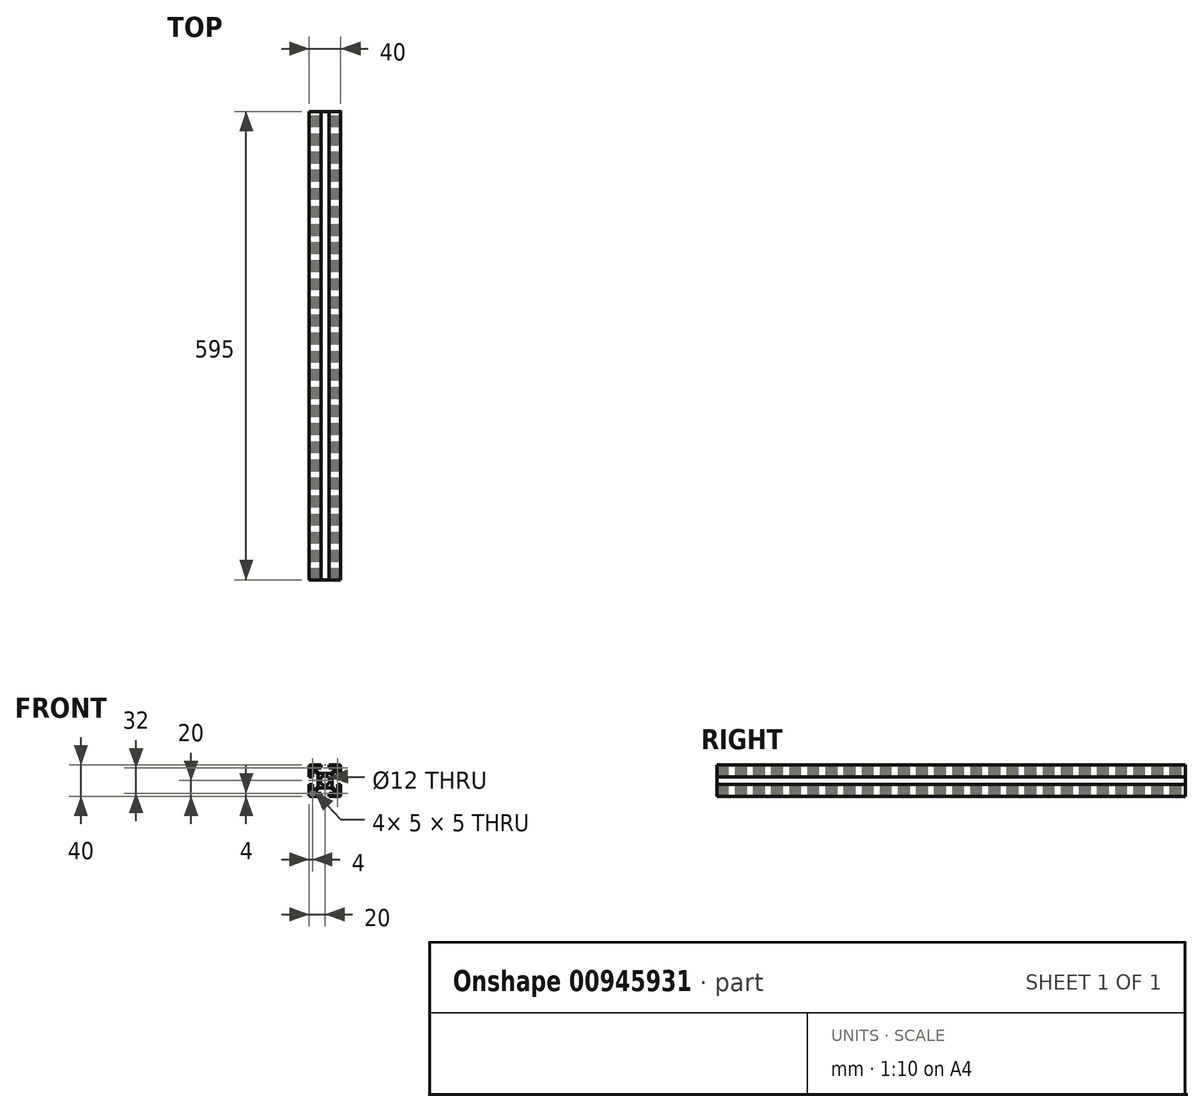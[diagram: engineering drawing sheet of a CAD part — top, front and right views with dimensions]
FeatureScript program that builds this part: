
annotation { "Feature Type Name" : "Feature", "Feature Type Description" : "" }
export const myFeature = defineFeature(function(context is Context, id is Id, definition is map)
    precondition{}
    {
        {
            var Q0;
            Q0=qCreatedBy(makeId("Front.planeOp"),FACE);
            var sketch = newSketch(context, id + "F0", { "sketchPlane" : qUnion([Q0])});
            skLineSegment(sketch, "E0.bottom", {"start": v(18, -20) * mm, "end": v(5, -20) * mm});
            skLineSegment(sketch, "E0.top", {"start": v(18, 20) * mm, "end": v(5, 20) * mm});
            skLineSegment(sketch, "E0.left", {"start": v(20, -18) * mm, "end": v(20, -5) * mm});
            skLineSegment(sketch, "E0.right", {"start": v(-20, -18) * mm, "end": v(-20, -5) * mm});
            skPoint(sketch, "E0.middle", {"position": v(0, 0) * mm});
            skLineSegment(sketch, "E1", {"start": v(0, 20) * mm, "end": v(0, -20) * mm, "construction": true});
            skLineSegment(sketch, "E2", {"start": v(-5, 20) * mm, "end": v(-5, 16) * mm});
            skLineSegment(sketch, "E3", {"start": v(-5, 16) * mm, "end": v(-11.5, 16) * mm});
            skCircle(sketch, "E4", {"center": v(0, 0) * mm, "radius": 6 * mm});
            skPoint(sketch, "E5.visualSharp", {"position": v(-20, 20) * mm});
            skArc(sketch, "E5.filletArc", {"start": v(-18, 20) * mm, "mid": v(-19.41, 19.41) * mm, "end": v(-20, 18) * mm});
            skPoint(sketch, "E6.visualSharp", {"position": v(20, 20) * mm});
            skArc(sketch, "E6.filletArc", {"start": v(20, 18) * mm, "mid": v(19.41, 19.41) * mm, "end": v(18, 20) * mm});
            skPoint(sketch, "E7.visualSharp", {"position": v(20, -20) * mm});
            skArc(sketch, "E7.filletArc", {"start": v(18, -20) * mm, "mid": v(19.41, -19.41) * mm, "end": v(20, -18) * mm});
            skPoint(sketch, "E8.visualSharp", {"position": v(-20, -20) * mm});
            skArc(sketch, "E8.filletArc", {"start": v(-20, -18) * mm, "mid": v(-19.41, -19.41) * mm, "end": v(-18, -20) * mm});
            skLineSegment(sketch, "E9", {"start": v(-7, 7) * mm, "end": v(-18, 18) * mm, "construction": true});
            skLineSegment(sketch, "E10.bottom", {"start": v(-13.5, 13.5) * mm, "end": v(-18.5, 13.5) * mm});
            skLineSegment(sketch, "E10.top", {"start": v(-13.5, 18.5) * mm, "end": v(-18.5, 18.5) * mm});
            skLineSegment(sketch, "E10.left", {"start": v(-13.5, 13.5) * mm, "end": v(-13.5, 18.5) * mm});
            skLineSegment(sketch, "E10.right", {"start": v(-18.5, 13.5) * mm, "end": v(-18.5, 18.5) * mm});
            skPoint(sketch, "E10.middle", {"position": v(-16, 16) * mm});
            skLineSegment(sketch, "E11.MirrorCS", {"start": v(5, 20) * mm, "end": v(5, 16) * mm});
            skLineSegment(sketch, "E12.MirrorCS", {"start": v(5, 16) * mm, "end": v(11.5, 16) * mm});
            skLineSegment(sketch, "E13.MirrorCS", {"start": v(13.5, 13.5) * mm, "end": v(18.5, 13.5) * mm});
            skLineSegment(sketch, "E14.MirrorCS", {"start": v(18.5, 13.5) * mm, "end": v(18.5, 18.5) * mm});
            skLineSegment(sketch, "E15.MirrorCS", {"start": v(13.5, 18.5) * mm, "end": v(18.5, 18.5) * mm});
            skLineSegment(sketch, "E16.MirrorCS", {"start": v(13.5, 13.5) * mm, "end": v(13.5, 18.5) * mm});
            skLineSegment(sketch, "E17", {"start": v(-20, 0) * mm, "end": v(20, 0) * mm, "construction": true});
            skLineSegment(sketch, "E18.trimOffspring", {"start": v(-5, 20) * mm, "end": v(-18, 20) * mm});
            skLineSegment(sketch, "E19", {"start": v(-11.5, 16) * mm, "end": v(-11.5, 12.91) * mm});
            skLineSegment(sketch, "E20", {"start": v(-11.5, 12.91) * mm, "end": v(-7.59, 9) * mm});
            skLineSegment(sketch, "E21", {"start": v(-7.59, 9) * mm, "end": v(0, 9) * mm});
            skLineSegment(sketch, "E22.MirrorCS", {"start": v(11.5, 16) * mm, "end": v(11.5, 12.91) * mm});
            skLineSegment(sketch, "E23.MirrorCS", {"start": v(11.5, 12.91) * mm, "end": v(7.59, 9) * mm});
            skLineSegment(sketch, "E24.MirrorCS", {"start": v(7.59, 9) * mm, "end": v(0, 9) * mm});
            skLineSegment(sketch, "E25.1.0", {"start": v(-20, -5) * mm, "end": v(-16, -5) * mm});
            skLineSegment(sketch, "E25.1.1", {"start": v(-16, -5) * mm, "end": v(-16, -11.5) * mm});
            skLineSegment(sketch, "E25.1.2", {"start": v(-16, -11.5) * mm, "end": v(-12.91, -11.5) * mm});
            skLineSegment(sketch, "E25.1.3", {"start": v(-12.91, -11.5) * mm, "end": v(-9, -7.59) * mm});
            skLineSegment(sketch, "E25.1.4", {"start": v(-9, -7.59) * mm, "end": v(-9, 0) * mm});
            skLineSegment(sketch, "E25.1.5", {"start": v(-9, 7.59) * mm, "end": v(-9, 0) * mm});
            skLineSegment(sketch, "E25.1.6", {"start": v(-12.91, 11.5) * mm, "end": v(-9, 7.59) * mm});
            skLineSegment(sketch, "E25.1.7", {"start": v(-16, 11.5) * mm, "end": v(-12.91, 11.5) * mm});
            skLineSegment(sketch, "E25.1.8", {"start": v(-16, 5) * mm, "end": v(-16, 11.5) * mm});
            skLineSegment(sketch, "E25.1.9", {"start": v(-20, 5) * mm, "end": v(-16, 5) * mm});
            skLineSegment(sketch, "E25.2.0", {"start": v(5, -20) * mm, "end": v(5, -16) * mm});
            skLineSegment(sketch, "E25.2.1", {"start": v(5, -16) * mm, "end": v(11.5, -16) * mm});
            skLineSegment(sketch, "E25.2.2", {"start": v(11.5, -16) * mm, "end": v(11.5, -12.91) * mm});
            skLineSegment(sketch, "E25.2.3", {"start": v(11.5, -12.91) * mm, "end": v(7.59, -9) * mm});
            skLineSegment(sketch, "E25.2.4", {"start": v(7.59, -9) * mm, "end": v(0, -9) * mm});
            skLineSegment(sketch, "E25.2.5", {"start": v(-7.59, -9) * mm, "end": v(0, -9) * mm});
            skLineSegment(sketch, "E25.2.6", {"start": v(-11.5, -12.91) * mm, "end": v(-7.59, -9) * mm});
            skLineSegment(sketch, "E25.2.7", {"start": v(-11.5, -16) * mm, "end": v(-11.5, -12.91) * mm});
            skLineSegment(sketch, "E25.2.8", {"start": v(-5, -16) * mm, "end": v(-11.5, -16) * mm});
            skLineSegment(sketch, "E25.2.9", {"start": v(-5, -20) * mm, "end": v(-5, -16) * mm});
            skLineSegment(sketch, "E26.2.3.0", {"start": v(20, 5) * mm, "end": v(16, 5) * mm});
            skLineSegment(sketch, "E26.3.3.0", {"start": v(16, 5) * mm, "end": v(16, 11.5) * mm});
            skLineSegment(sketch, "E26.6.3.0", {"start": v(16, 11.5) * mm, "end": v(12.91, 11.5) * mm});
            skLineSegment(sketch, "E26.9.3.0", {"start": v(12.91, 11.5) * mm, "end": v(9, 7.59) * mm});
            skLineSegment(sketch, "E26.12.3.0", {"start": v(9, 7.59) * mm, "end": v(9, 0) * mm});
            skLineSegment(sketch, "E26.15.3.0", {"start": v(9, -7.59) * mm, "end": v(9, 0) * mm});
            skLineSegment(sketch, "E26.18.3.0", {"start": v(12.91, -11.5) * mm, "end": v(9, -7.59) * mm});
            skLineSegment(sketch, "E26.21.3.0", {"start": v(16, -11.5) * mm, "end": v(12.91, -11.5) * mm});
            skLineSegment(sketch, "E26.24.3.0", {"start": v(16, -5) * mm, "end": v(16, -11.5) * mm});
            skLineSegment(sketch, "E26.27.3.0", {"start": v(20, -5) * mm, "end": v(16, -5) * mm});
            skLineSegment(sketch, "E27.trimOffspring", {"start": v(-20, 5) * mm, "end": v(-20, 18) * mm});
            skLineSegment(sketch, "E28.trimOffspring", {"start": v(-5, -20) * mm, "end": v(-18, -20) * mm});
            skLineSegment(sketch, "E29.trimOffspring", {"start": v(20, 5) * mm, "end": v(20, 18) * mm});
            skLineSegment(sketch, "E30.MirrorCS", {"start": v(-18.5, -13.5) * mm, "end": v(-18.5, -18.5) * mm});
            skLineSegment(sketch, "E31.MirrorCS", {"start": v(-13.5, -18.5) * mm, "end": v(-18.5, -18.5) * mm});
            skLineSegment(sketch, "E32.MirrorCS", {"start": v(-13.5, -13.5) * mm, "end": v(-13.5, -18.5) * mm});
            skLineSegment(sketch, "E33.MirrorCS", {"start": v(-13.5, -13.5) * mm, "end": v(-18.5, -13.5) * mm});
            skLineSegment(sketch, "E34.MirrorCS", {"start": v(13.5, -13.5) * mm, "end": v(13.5, -18.5) * mm});
            skLineSegment(sketch, "E35.MirrorCS", {"start": v(13.5, -18.5) * mm, "end": v(18.5, -18.5) * mm});
            skLineSegment(sketch, "E36.MirrorCS", {"start": v(18.5, -13.5) * mm, "end": v(18.5, -18.5) * mm});
            skLineSegment(sketch, "E37.MirrorCS", {"start": v(13.5, -13.5) * mm, "end": v(18.5, -13.5) * mm});
            skSolve(sketch);
        }
        {
            var Q0;
            Q0=makeQuery(id+"F0.imprint","IMPRINT",FACE,{"disambiguationData":[TD([[makeQuery(id+"F0.imprint","IMPRINT",EDGE,{"derivedFrom":sQuery(id+"F0.wireOp",EDGE,"E0.bottom")}),-1.0]])]});
            extrude(context, id + "F1", {"entities" : qUnion([Q0]), "depth" : 595 * mm, "offsetDistance" : 25 * mm});
        }
    });
